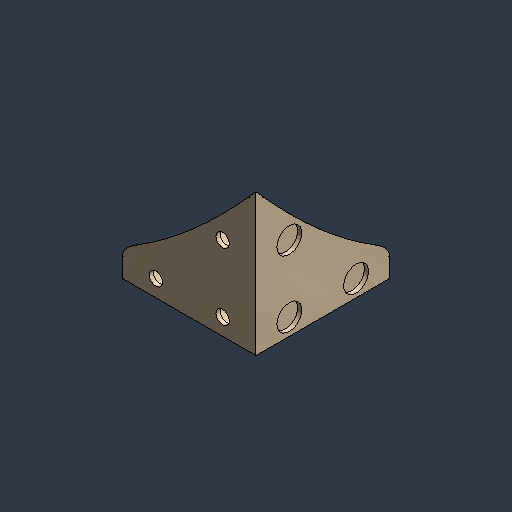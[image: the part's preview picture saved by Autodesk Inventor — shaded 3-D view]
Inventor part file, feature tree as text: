
AUTODESK INVENTOR PART (.ipt)
format: ipt  version: 2024.3 (Build 283343000, 343)  size: 166,912 bytes
history: native  units: mm (DEFAULTED — no unit token found)
features: sketch x9, other x3, plane x1
ambient origin geometry x8: Origin, YZ Plane, XZ Plane, XY Plane, X Axis, Y Axis, Z Axis, Center Point
bodies: Solid1 (feature_tree)
feature tree (13):
  other  "hopper_fin.ipt"
  other  "Solid1::hopper_fin.ipt"
  other  "TaggingFeature1"
  sketch  "Sketch1"  dims[d0=10.0mm]
  sketch  "Sketch2"
  sketch  "Sketch3"
  sketch  "Sketch4"
  sketch  "Sketch5"
  sketch  "Sketch6"
  sketch  "Sketch7"
  sketch  "Sketch8"
  sketch  "Sketch9"
  plane  "Work Plane1"
